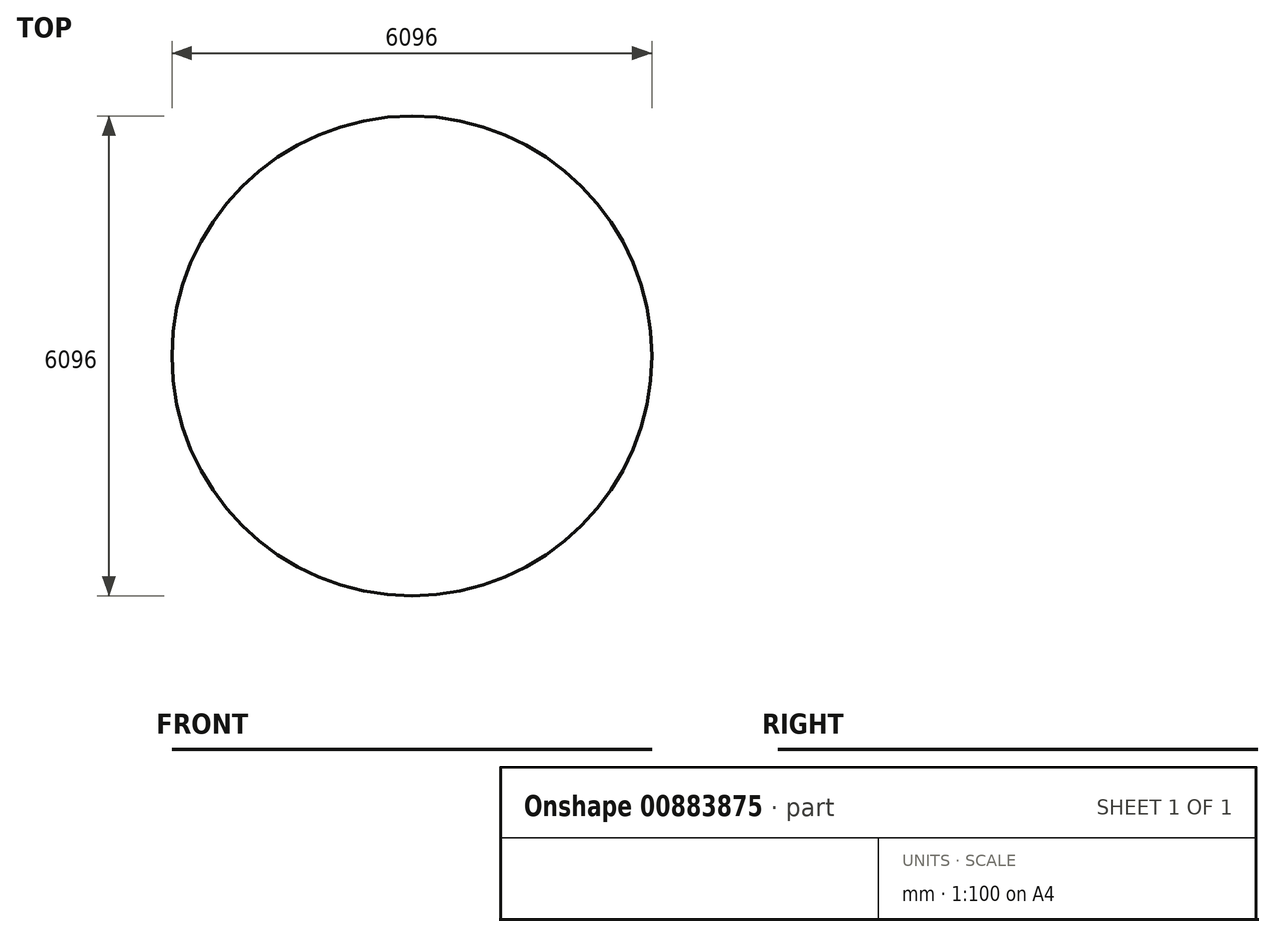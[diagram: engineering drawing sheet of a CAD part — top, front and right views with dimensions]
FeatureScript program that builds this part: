
annotation { "Feature Type Name" : "Feature", "Feature Type Description" : "" }
export const myFeature = defineFeature(function(context is Context, id is Id, definition is map)
    precondition{}
    {
        {
            var Q0;
            Q0=qCreatedBy(makeId("Top.planeOp"),FACE);
            var sketch = newSketch(context, id + "F0", { "sketchPlane" : qUnion([Q0])});
            skCircle(sketch, "E0", {"center": v(0, 0) * mm, "radius": 3048 * mm});
            skSolve(sketch);
        }
        {
            var Q0;
            Q0=makeQuery(id+"F0.imprint","IMPRINT",FACE,{"disambiguationData":[TD([[makeQuery(id+"F0.imprint","IMPRINT",EDGE,{"derivedFrom":sQuery(id+"F0.wireOp",EDGE,"E0")}),1.0]])]});
            extrude(context, id + "F1", {"entities" : qUnion([Q0]), "depth" : 1 / 812.8 * mm, "offsetDistance" : 30.48 * mm});
        }
    });
